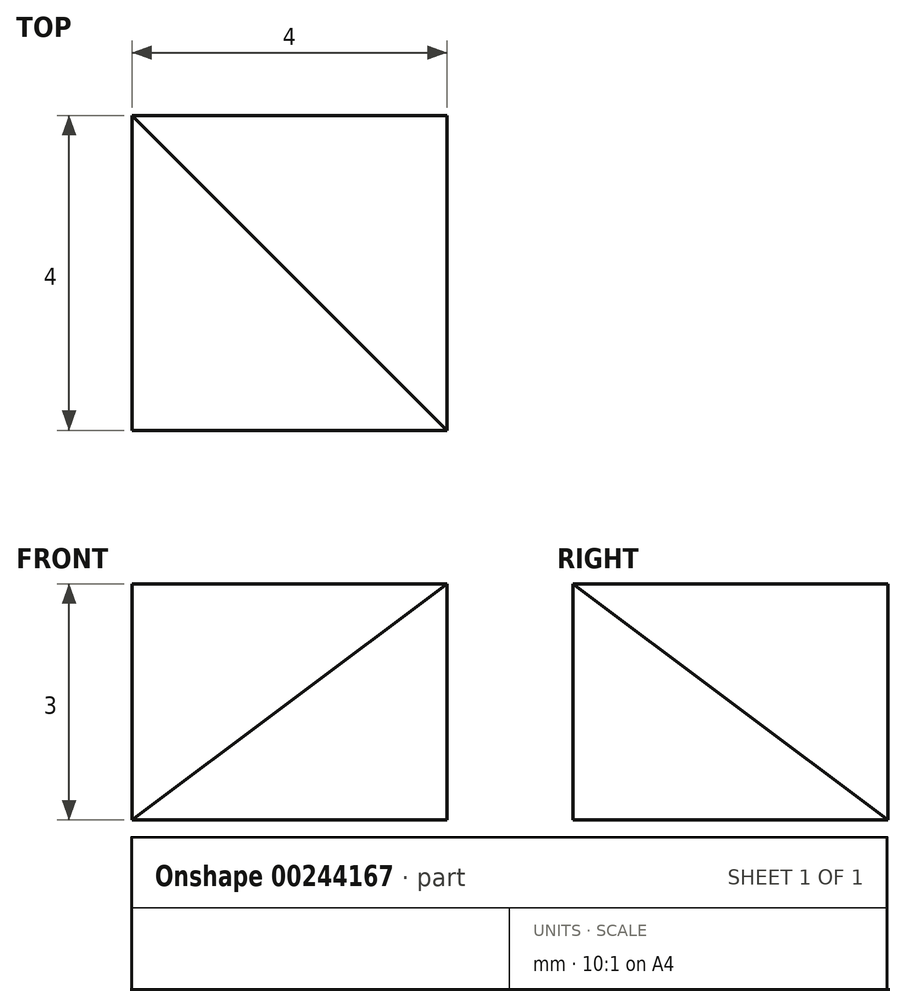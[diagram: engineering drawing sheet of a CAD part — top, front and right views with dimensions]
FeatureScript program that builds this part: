
annotation { "Feature Type Name" : "Feature", "Feature Type Description" : "" }
export const myFeature = defineFeature(function(context is Context, id is Id, definition is map)
    precondition{}
    {
        {
            var Q0;
            Q0=qCreatedBy(makeId("Top.planeOp"),FACE);
            var sketch = newSketch(context, id + "F0", { "sketchPlane" : qUnion([Q0])});
            skLineSegment(sketch, "E0.bottom", {"start": v(0, 0) * mm, "end": v(4, 0) * mm});
            skLineSegment(sketch, "E0.top", {"start": v(0, 4) * mm, "end": v(4, 4) * mm});
            skLineSegment(sketch, "E0.left", {"start": v(0, 0) * mm, "end": v(0, 4) * mm});
            skLineSegment(sketch, "E0.right", {"start": v(4, 0) * mm, "end": v(4, 4) * mm});
            skSolve(sketch);
        }
        {
            var Q0;
            Q0 = qSketchRegion(id + "F0", true);
            extrude(context, id + "F1", {"entities" : qUnion([Q0]), "depth" : 3 * mm});
        }
        {
            var Q0;
            Q0=qCreatedBy(makeId("Origin.pointOp"),VERTEX);
            var Q1;
            Q1=makeQuery(id+"F1.opExtrude","CAP_VERTEX",VERTEX,{"disambiguationData":[OSD([sQuery(id+"F0.wireOp",EDGE,"E0.bottom"),sQuery(id+"F0.wireOp",EDGE,"E0.right")])],"isStart":false});
            var Q2;
            Q2=makeQuery(id+"F1.opExtrude","CAP_VERTEX",VERTEX,{"disambiguationData":[OSD([sQuery(id+"F0.wireOp",EDGE,"E0.top"),sQuery(id+"F0.wireOp",EDGE,"E0.left")])],"isStart":false});
            cPlane(context, id + "F2", {"entities" : qUnion([Q0, Q1, Q2]), "cplaneType" : CPlaneType.THREE_POINT, "offset" : 25 * mm, "width" : 150 * mm, "height" : 150 * mm});
        }
        {
            var Q0;
            Q0=qCreatedBy(id+"F2.planeOp",FACE);
            var sketch = newSketch(context, id + "F3", { "sketchPlane" : qUnion([Q0])});
            skLineSegment(sketch, "E1.bottom", {"start": v(-4.2, -6.72) * mm, "end": v(13.39, -6.72) * mm});
            skLineSegment(sketch, "E1.top", {"start": v(-4.2, 4.72) * mm, "end": v(13.39, 4.72) * mm});
            skLineSegment(sketch, "E1.left", {"start": v(-4.2, -6.72) * mm, "end": v(-4.2, 4.72) * mm});
            skLineSegment(sketch, "E1.right", {"start": v(13.39, -6.72) * mm, "end": v(13.39, 4.72) * mm});
            skSolve(sketch);
        }
        {
            var Q0;
            Q0 = qSketchRegion(id + "F3", true);
            extrude(context, id + "F4", {"entities" : qUnion([Q0]), "operationType" : NewBodyOperationType.REMOVE, "oppositeDirection" : true, "depth" : 25 * mm});
        }
        {
            var Q0;
            Q0=makeQuery(id+"F1.opExtrude","CAP_VERTEX",VERTEX,{"disambiguationData":[OSD([sQuery(id+"F0.wireOp",EDGE,"E0.top"),sQuery(id+"F0.wireOp",EDGE,"E0.left")])],"isStart":false});
            var Q1;
            Q1=makeQuery(id+"F1.opExtrude","CAP_VERTEX",VERTEX,{"disambiguationData":[OSD([sQuery(id+"F0.wireOp",EDGE,"E0.top"),sQuery(id+"F0.wireOp",EDGE,"E0.right")])],"isStart":true});
            var Q2;
            Q2=makeQuery(id+"F1.opExtrude","CAP_VERTEX",VERTEX,{"disambiguationData":[OSD([sQuery(id+"F0.wireOp",EDGE,"E0.bottom"),sQuery(id+"F0.wireOp",EDGE,"E0.right")])],"isStart":false});
            cPlane(context, id + "F5", {"entities" : qUnion([Q0, Q1, Q2]), "cplaneType" : CPlaneType.THREE_POINT, "offset" : 25 * mm, "width" : 150 * mm, "height" : 150 * mm});
        }
        {
            var Q0;
            Q0=qCreatedBy(id+"F5.planeOp",FACE);
            var sketch = newSketch(context, id + "F6", { "sketchPlane" : qUnion([Q0])});
            skLineSegment(sketch, "E2.bottom", {"start": v(-7.46, 5.21) * mm, "end": v(15.26, 5.21) * mm});
            skLineSegment(sketch, "E2.top", {"start": v(-7.46, -5.8) * mm, "end": v(15.26, -5.8) * mm});
            skLineSegment(sketch, "E2.left", {"start": v(-7.46, 5.21) * mm, "end": v(-7.46, -5.8) * mm});
            skLineSegment(sketch, "E2.right", {"start": v(15.26, 5.21) * mm, "end": v(15.26, -5.8) * mm});
            skSolve(sketch);
        }
        {
            var Q0;
            Q0 = qSketchRegion(id + "F6", true);
            extrude(context, id + "F7", {"entities" : qUnion([Q0]), "operationType" : NewBodyOperationType.REMOVE, "depth" : 25 * mm});
        }
    });
